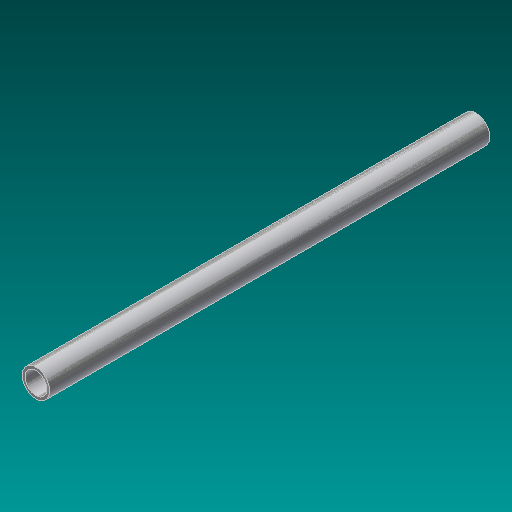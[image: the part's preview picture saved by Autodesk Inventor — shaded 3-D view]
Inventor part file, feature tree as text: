
AUTODESK INVENTOR PART (.ipt)
format: ipt  version: 2017 (Build 210142000, 142)  size: 104,960 bytes
history: native  units: in
note: dims shown in document units (in); Inventor stores cm internally (conversion verified against a paired STEP export)
features: extrude x1, sketch x1
ambient origin geometry x8: Origin, YZ Plane, XZ Plane, XY Plane, X Axis, Y Axis, Z Axis, Center Point
bodies: Solid1 (feature_tree)
feature tree (2):
  extrude  "Extrusion1"  Depth=30.25in
  sketch  "Sketch1"  dims[d0=1.9in d1=1.5in d2=30.25in d3=0.0in]
